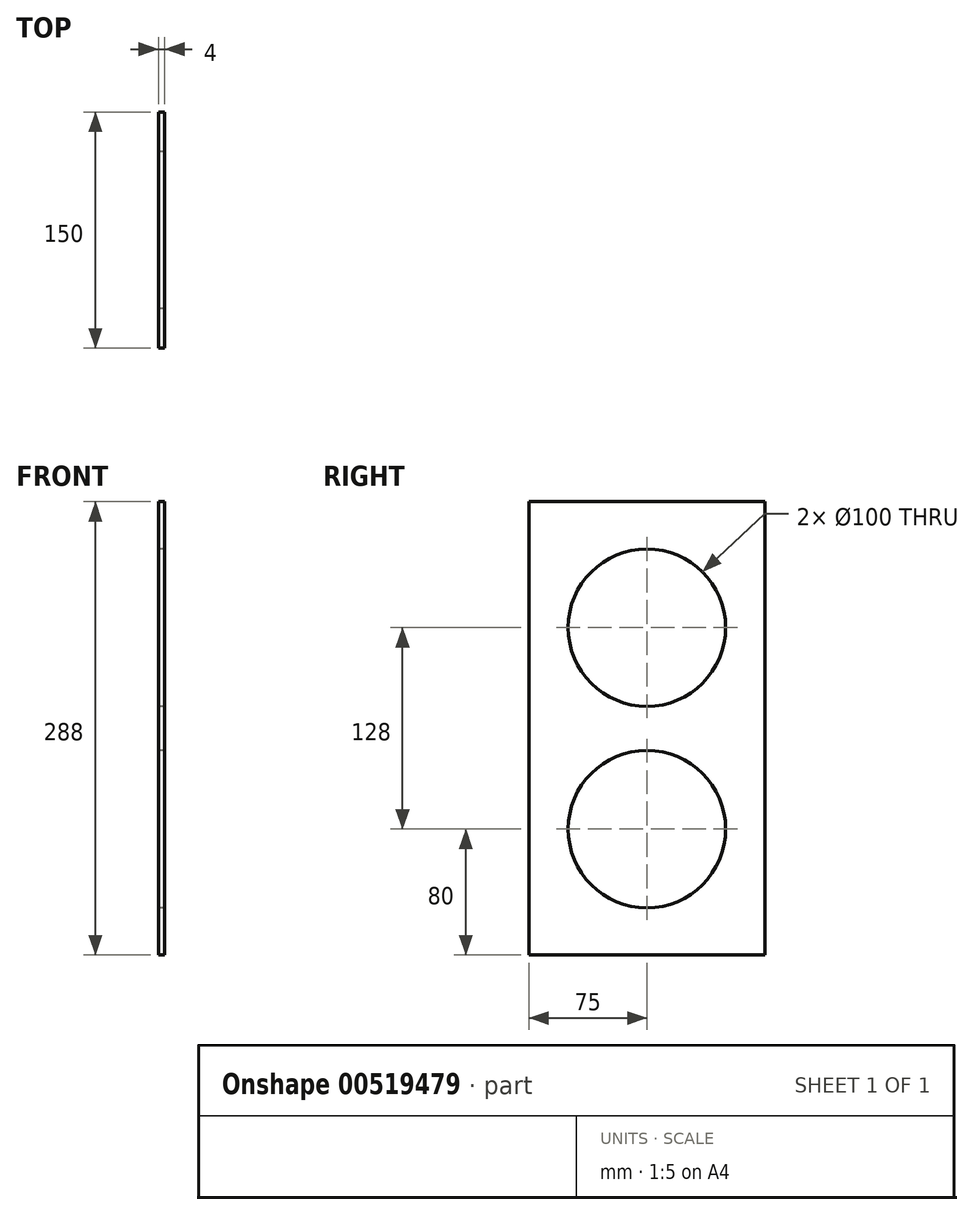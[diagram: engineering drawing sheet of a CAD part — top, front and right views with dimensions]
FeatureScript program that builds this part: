
annotation { "Feature Type Name" : "Feature", "Feature Type Description" : "" }
export const myFeature = defineFeature(function(context is Context, id is Id, definition is map)
    precondition{}
    {
        {
            var Q0;
            Q0=qCreatedBy(makeId("Right.planeOp"),FACE);
            var sketch = newSketch(context, id + "F0", { "sketchPlane" : qUnion([Q0])});
            skLineSegment(sketch, "E0", {"start": v(0, 0) * mm, "end": v(150, 0) * mm});
            skLineSegment(sketch, "E1", {"start": v(150, 0) * mm, "end": v(150, 288) * mm});
            skLineSegment(sketch, "E2", {"start": v(0, 288) * mm, "end": v(0, 0) * mm});
            skLineSegment(sketch, "E3", {"start": v(0, 288) * mm, "end": v(150, 288) * mm});
            skCircle(sketch, "E4", {"center": v(75, 208) * mm, "radius": 50 * mm});
            skCircle(sketch, "E5", {"center": v(75, 80) * mm, "radius": 50 * mm});
            skPoint(sketch, "E6", {"position": v(75, 288) * mm});
            skPoint(sketch, "E7", {"position": v(75, 0) * mm});
            skSolve(sketch);
        }
        {
            var Q0;
            Q0 = qSketchRegion(id + "F0", true);
            extrude(context, id + "F1", {"entities" : qUnion([Q0]), "depth" : 4 * mm, "offsetDistance" : 25 * mm});
        }
    });
